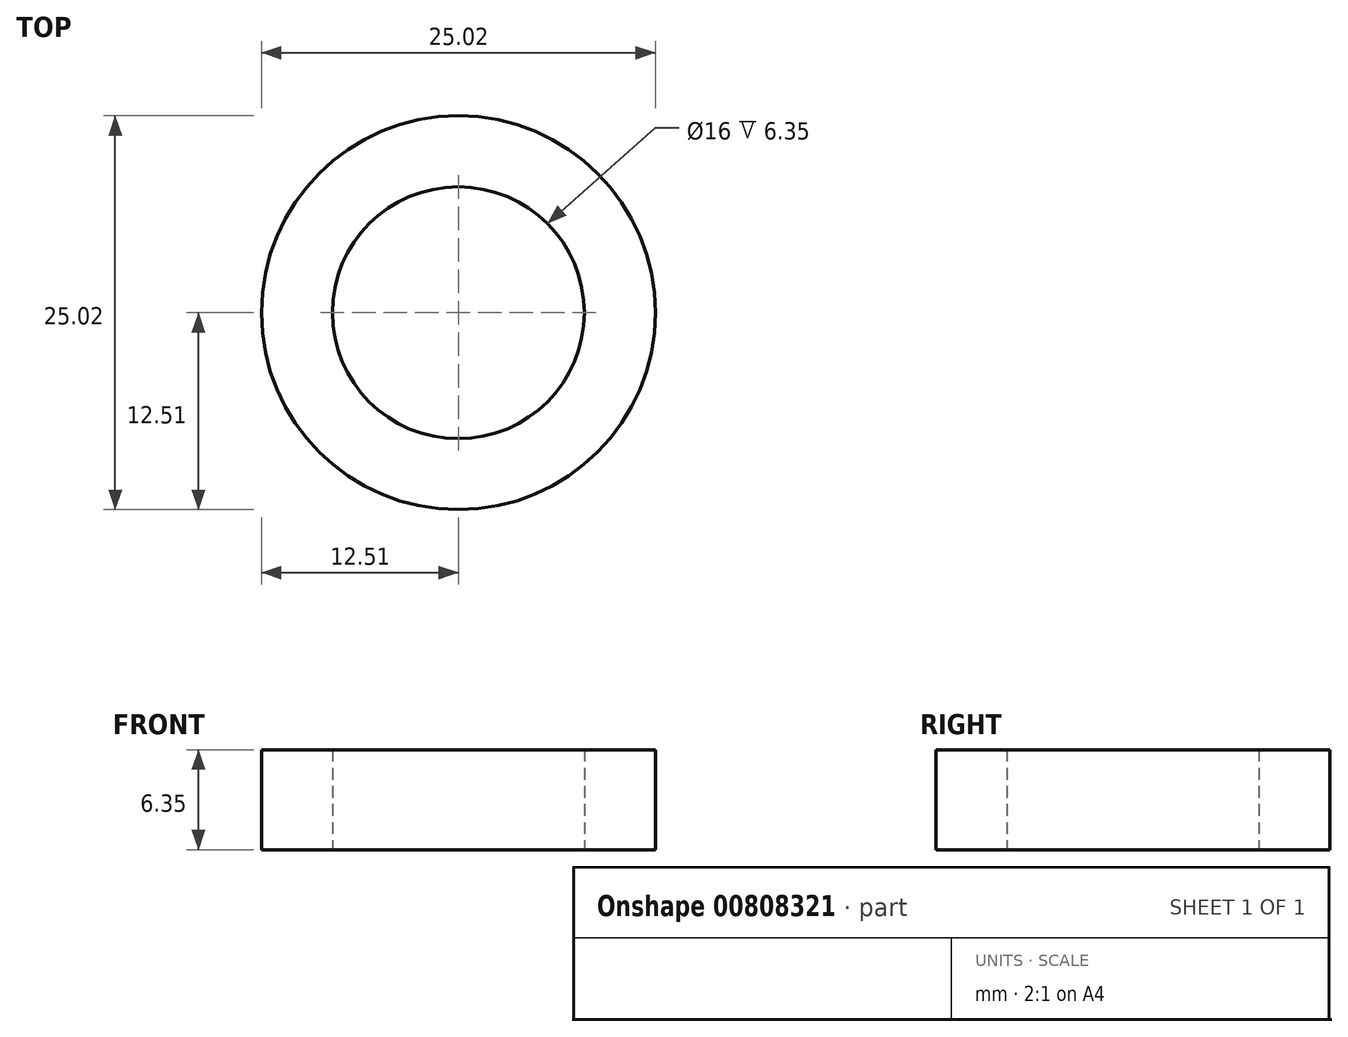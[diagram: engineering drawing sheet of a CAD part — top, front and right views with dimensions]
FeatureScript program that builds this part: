
annotation { "Feature Type Name" : "Feature", "Feature Type Description" : "" }
export const myFeature = defineFeature(function(context is Context, id is Id, definition is map)
    precondition{}
    {
        {
            var Q0;
            Q0=qCreatedBy(makeId("Top.planeOp"),FACE);
            var sketch = newSketch(context, id + "F0", { "sketchPlane" : qUnion([Q0])});
            skCircle(sketch, "E0", {"center": v(0, 0) * mm, "radius": 12.5 * mm});
            skCircle(sketch, "E1", {"center": v(0, 0) * mm, "radius": 8 * mm});
            skSolve(sketch);
        }
        {
            var Q0;
            Q0 = qSketchRegion(id + "F0", true);
            extrude(context, id + "F1", {"entities" : qUnion([Q0]), "depth" : 6.35 * mm, "offsetDistance" : 25.4 * mm});
        }
    });
